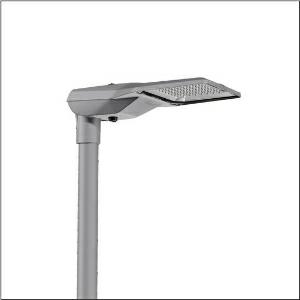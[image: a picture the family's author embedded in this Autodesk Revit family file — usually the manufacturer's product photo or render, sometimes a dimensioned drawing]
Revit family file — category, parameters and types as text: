
# Revit family: streetlight_sl_21_midi___st1_5a_5xe3p43t08lb_4b54
name_source: partatom
category: Lighting Fixtures
units: mm (PartAtom-declared; Revit-internal decimal feet)

## family parameters
Cut with Voids When Loaded = No
Host = Face
Light Source = No
Part Type = Normal
Room Calculation Point = No
Round Connector Dimension = Use Diameter
Shared = No

## types (1)
- --- (1 x LED, 14690 lm, 99.6 W, 4000K)
    Apparent Load = 100 VA
    CIE Flux Codes = 22 53 95 100 100
    Color Rendering = 70
    Color Temperature = 4000K
    Default Elevation = 1800 mm
    Description = Streetlight SL 21 midi, mast luminaire, primary light control with lens, of PMMA, primary optical cover: cover, of toughened safety glass, transparent, light distribution: ST1.5a, light emission: direct distribution, primary light characteristic: asymmetric, installation type: side-entry, post-top, LED, High Power LED, rated luminous flux: 14.690lm, luminous efficacy: 148lm/W, light colour: 740, colour temperature: 4000K, control gear: D4i, control: overheat protection, constant luminous flux control, time-dependent luminous flux control, flexible luminous flux parameterisation, pre-setting: logarithmic dimming characteristic, mains connection: 230..240V, AC, 50/60Hz, start of lifetime: 100W, end of service life: 102W, reduction: 46W, luminaire housing, of diecast aluminium, powder-coated, SITECO metallic grey (DB 702S), corrosivity category C5 high according to DIN EN ISO 12944, please order mast flange separately, inclination adjustable: 0°, 5°, 10°, 15°, sealing non-destructively replaceable, multi-level sealing system, length: 644mm, width: 335mm, height: 110mm, mast flange for spigot size: 42mm (side-entry): 5XC10008XM4, 60/48mm (side-entry/post-top): 5XC10108XM2, 76/60mm (side-entry/post-top): 5XC10108XM1, mounting height: 4..8m, Smart Interface below and above, protection rating (complete): IP66, insulation class (complete): insulation class II (safety insulation), certification: CE, ENEC, ENEC+, VDE, impact resistance: IK10, permissible operating ambient temperature for outdoor applications: -40..+50°C, standard-compliant lighting for roads and squares, packaging unit: 1 piece

Light Distribution: ST1.5a
    Height = 111 mm
    Lamp = 1 x LED
    Lamp Light Flux = 14690 lm
    Lamp Power = 99.6 W
    Lamp count = 1
    Length = 644 mm
    Luminous efficacy = 147 lm/W
    Manufacturer = Siteco
    ModVariant = No
    Model = 5XE3P43T08LB
    Number of Poles = 1
    OnlyDefault = Yes
    Power Factor = 1
    Product Name = Streetlight SL 21 midi | ST1.5a
    Product group = mast luminaire | pylon top
    ProductGroupID = 6100
    Protection Class = Protection class II
    Protection Degree = IP 66
    RLX_Detail_Level = 1
    RLX_Emergency_Light_Flux = 0 lm
    RLX_Emergency_Type = 0
    RLX_Emergency_Type_DB = No
    RlxData = <blob elided: 30473 chars, md5=2c991f47>
    Socket = socket
    Standby Power = 0 W
    System Light Flux = 14690 lm
    System Power = 100 W
    Type Comments = factory setting: luminous flux: 100 % | dim-lin: 254 | 1020 mA
    Type Image = l_1004304.jpg
    URL = http://relux.com
    VarID = @adj_032415
    Voltage = 0 V
    Weight = 0.00 kg
    Width = 336 mm

## geometry (parser evidence)
native form markers: Blend x4, Sweep x9
no freeform markers — native parametric forms only
